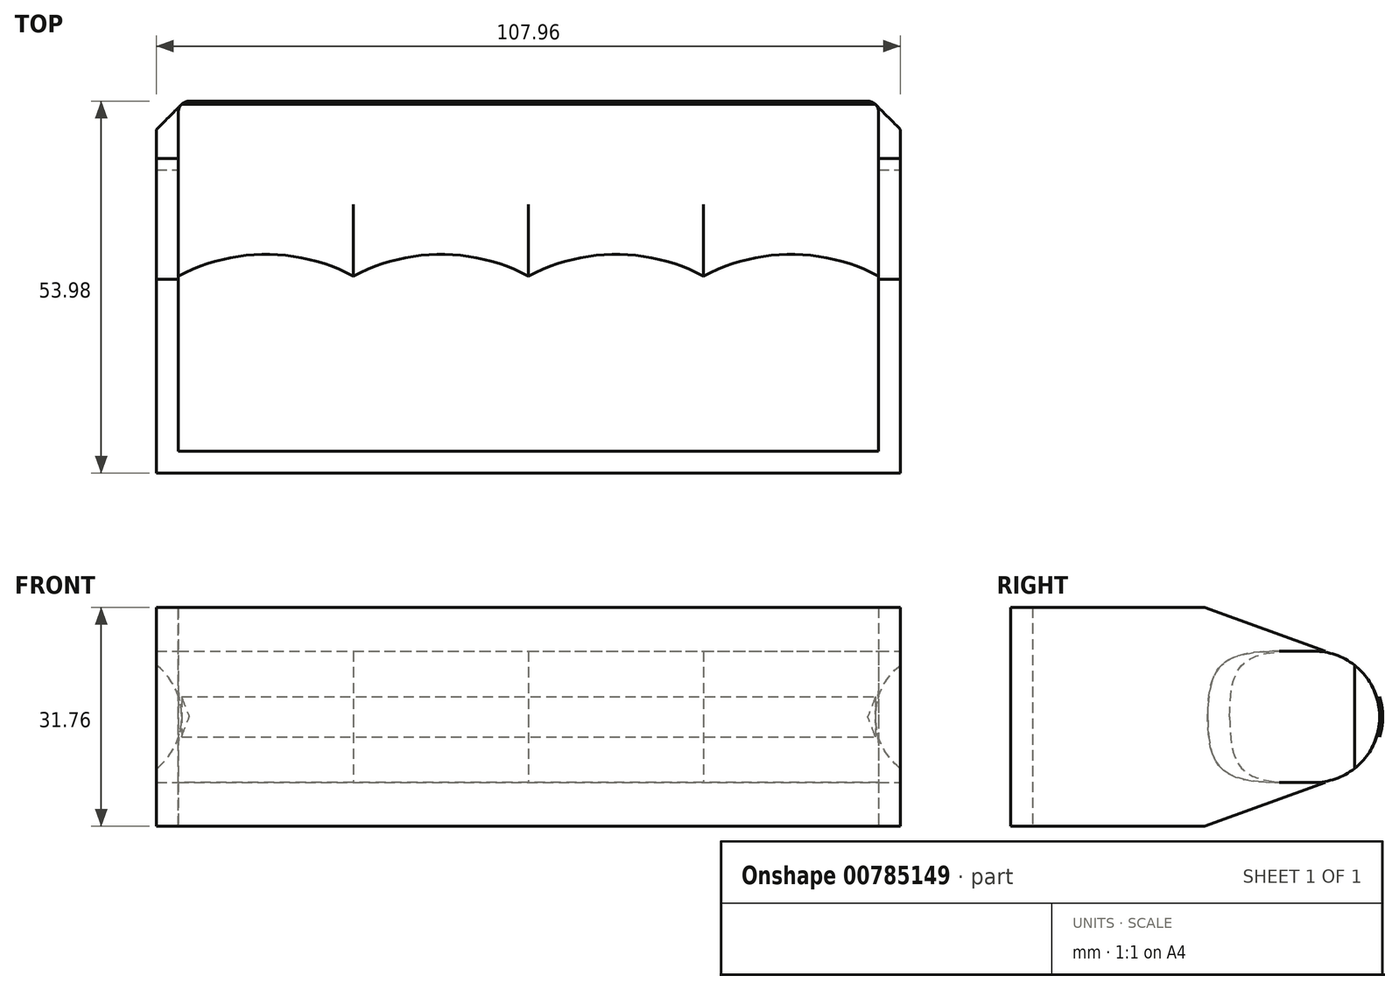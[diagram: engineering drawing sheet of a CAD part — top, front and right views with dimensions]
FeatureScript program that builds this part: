
annotation { "Feature Type Name" : "Feature", "Feature Type Description" : "" }
export const myFeature = defineFeature(function(context is Context, id is Id, definition is map)
    precondition{}
    {
        {
            var Q0;
            Q0=qCreatedBy(makeId("Top.planeOp"),FACE);
            var sketch = newSketch(context, id + "F0", { "sketchPlane" : qUnion([Q0])});
            skLineSegment(sketch, "E0.bottom", {"start": v(50.8, 25.4) * mm, "end": v(-50.8, 25.4) * mm, "construction": true});
            skLineSegment(sketch, "E0.top", {"start": v(49.21, 50.8) * mm, "end": v(-49.21, 50.8) * mm});
            skLineSegment(sketch, "E0.left", {"start": v(50.8, 25.4) * mm, "end": v(50.8, 49.21) * mm});
            skLineSegment(sketch, "E0.right", {"start": v(-50.8, 25.4) * mm, "end": v(-50.8, 49.21) * mm});
            skPoint(sketch, "E0.middle", {"position": v(0, 38.1) * mm});
            skPoint(sketch, "E1.visualSharp", {"position": v(50.8, 50.8) * mm});
            skArc(sketch, "E1.filletArc", {"start": v(50.8, 49.21) * mm, "mid": v(50.34, 50.34) * mm, "end": v(49.21, 50.8) * mm});
            skPoint(sketch, "E2.visualSharp", {"position": v(-50.8, 50.8) * mm});
            skArc(sketch, "E2.filletArc", {"start": v(-49.21, 50.8) * mm, "mid": v(-50.34, 50.34) * mm, "end": v(-50.8, 49.21) * mm});
            skArc(sketch, "E3", {"start": v(50.8, 25.4) * mm, "mid": v(38.1, 28.58) * mm, "end": v(25.4, 25.4) * mm});
            skArc(sketch, "E4", {"start": v(25.4, 25.4) * mm, "mid": v(12.7, 28.57) * mm, "end": v(0, 25.4) * mm});
            skArc(sketch, "E5", {"start": v(0, 25.4) * mm, "mid": v(-12.7, 28.57) * mm, "end": v(-25.4, 25.4) * mm});
            skArc(sketch, "E6", {"start": v(-50.8, 25.4) * mm, "mid": v(-38.1, 28.57) * mm, "end": v(-25.4, 25.4) * mm});
            skLineSegment(sketch, "E7.left", {"start": v(-50.8, 49.21) * mm, "end": v(-50.8, 0) * mm});
            skLineSegment(sketch, "E7.right", {"start": v(-53.98, 46.7) * mm, "end": v(-53.97, 0) * mm});
            skLineSegment(sketch, "E8.right", {"start": v(53.98, 46.7) * mm, "end": v(53.98, 0) * mm});
            skLineSegment(sketch, "E9.bottom", {"start": v(-50.8, 0) * mm, "end": v(50.8, 0) * mm});
            skLineSegment(sketch, "E9.top", {"start": v(-53.97, -3.17) * mm, "end": v(53.98, -3.17) * mm});
            skLineSegment(sketch, "E9.left", {"start": v(-53.97, 0) * mm, "end": v(-53.97, -3.17) * mm});
            skLineSegment(sketch, "E9.right", {"start": v(53.98, 0) * mm, "end": v(53.98, -3.17) * mm});
            skLineSegment(sketch, "E10", {"start": v(50.34, 50.34) * mm, "end": v(53.98, 46.7) * mm});
            skLineSegment(sketch, "E11.trimOffspring", {"start": v(50.8, 49.21) * mm, "end": v(50.8, 0) * mm});
            skLineSegment(sketch, "E12", {"start": v(-50.34, 50.34) * mm, "end": v(-53.98, 46.7) * mm});
            skSolve(sketch);
        }
        {
            var Q0;
            {var subQ6=sQuery(id+"F0.wireOp",EDGE,"E0.top");Q0=makeQuery(id+"F0.imprint","IMPRINT",FACE,{"disambiguationData":[TD([[makeQuery(id+"F0.imprint","IMPRINT",EDGE,{"derivedFrom":subQ6}),1.0]])]});}
            extrude(context, id + "F1", {"entities" : qUnion([Q0]), "depth" : 9.52 * mm, "offsetDistance" : 25.4 * mm, "hasSecondDirection" : true, "secondDirectionOppositeDirection" : true, "secondDirectionDepth" : 9.52 * mm});
        }
        {
            var Q0;
            Q0=makeQuery(id+"F0.imprint","IMPRINT",FACE,{"disambiguationData":[TD([[makeQuery(id+"F0.imprint","IMPRINT",EDGE,{"derivedFrom":sQuery(id+"F0.wireOp",EDGE,"E7.right")}),1.0]])]});
            extrude(context, id + "F2", {"entities" : qUnion([Q0]), "depth" : 15.88 * mm, "offsetDistance" : 25.4 * mm, "hasSecondDirection" : true, "secondDirectionOppositeDirection" : true, "secondDirectionDepth" : 15.88 * mm});
        }
        {
            var Q0;
            Q0=makeQuery(id+"F1.opExtrude","CAP_EDGE",EDGE,{"disambiguationData":[OSD([sQuery(id+"F0.wireOp",EDGE,"E0.top")])],"isStart":false});
            var Q1;
            Q1=makeQuery(id+"F1.opExtrude","CAP_EDGE",EDGE,{"disambiguationData":[OSD([sQuery(id+"F0.wireOp",EDGE,"E0.top")])],"isStart":true});
            fillet(context, id + "F3", {"entities" : qUnion([Q0, Q1]), "radius" : 9.52 * mm, "allowEdgeOverflow" : false});
        }
        {
            var Q0;
            Q0=makeQuery(id+"F1.opExtrude","CAP_EDGE",EDGE,{"disambiguationData":[OSD([sQuery(id+"F0.wireOp",EDGE,"E5")])],"isStart":true});
            var Q1;
            Q1=makeQuery(id+"F1.opExtrude","CAP_EDGE",EDGE,{"disambiguationData":[OSD([sQuery(id+"F0.wireOp",EDGE,"E6")])],"isStart":true});
            var Q2;
            Q2=makeQuery(id+"F1.opExtrude","CAP_EDGE",EDGE,{"disambiguationData":[OSD([sQuery(id+"F0.wireOp",EDGE,"E6")])],"isStart":false});
            var Q3;
            Q3=makeQuery(id+"F1.opExtrude","CAP_EDGE",EDGE,{"disambiguationData":[OSD([sQuery(id+"F0.wireOp",EDGE,"E5")])],"isStart":false});
            var Q4;
            Q4=makeQuery(id+"F1.opExtrude","CAP_EDGE",EDGE,{"disambiguationData":[OSD([sQuery(id+"F0.wireOp",EDGE,"E4")])],"isStart":true});
            var Q5;
            Q5=makeQuery(id+"F1.opExtrude","CAP_EDGE",EDGE,{"disambiguationData":[OSD([sQuery(id+"F0.wireOp",EDGE,"E4")])],"isStart":false});
            var Q6;
            Q6=makeQuery(id+"F1.opExtrude","CAP_EDGE",EDGE,{"disambiguationData":[OSD([sQuery(id+"F0.wireOp",EDGE,"E3")])],"isStart":true});
            var Q7;
            Q7=makeQuery(id+"F1.opExtrude","CAP_EDGE",EDGE,{"disambiguationData":[OSD([sQuery(id+"F0.wireOp",EDGE,"E3")])],"isStart":false});
            fillet(context, id + "F4", {"entities" : qUnion([Q0, Q1, Q2, Q3, Q4, Q5, Q6, Q7]), "radius" : 9.52 * mm, "rho" : 0.6, "crossSection" : FilletCrossSection.CONIC, "allowEdgeOverflow" : false});
        }
        {
            var Q0;
            Q0=qCreatedBy(makeId("Right.planeOp"),FACE);
            var sketch = newSketch(context, id + "F5", { "sketchPlane" : qUnion([Q0])});
            skLineSegment(sketch, "E13.bottom", {"start": v(50.34, 9.53) * mm, "end": v(24.94, 9.52) * mm});
            skLineSegment(sketch, "E13.top", {"start": v(50.34, 15.88) * mm, "end": v(24.94, 15.88) * mm});
            skLineSegment(sketch, "E13.left", {"start": v(50.34, 9.53) * mm, "end": v(50.34, 15.88) * mm});
            skLineSegment(sketch, "E13.right", {"start": v(24.94, 9.52) * mm, "end": v(24.94, 15.87) * mm, "construction": true});
            skLineSegment(sketch, "E14.bottom", {"start": v(50.34, -9.52) * mm, "end": v(24.94, -9.53) * mm});
            skLineSegment(sketch, "E14.top", {"start": v(50.34, -15.88) * mm, "end": v(24.94, -15.88) * mm});
            skLineSegment(sketch, "E14.left", {"start": v(50.34, -9.52) * mm, "end": v(50.34, -15.88) * mm});
            skLineSegment(sketch, "E14.right", {"start": v(24.94, -9.53) * mm, "end": v(24.94, -15.88) * mm, "construction": true});
            skArc(sketch, "E15", {"start": v(40.82, -9.53) * mm, "mid": v(50.34, 0) * mm, "end": v(40.82, 9.53) * mm});
            skLineSegment(sketch, "E16", {"start": v(50.34, 9.53) * mm, "end": v(50.34, -9.52) * mm});
            skLineSegment(sketch, "E17", {"start": v(44.06, 8.96) * mm, "end": v(24.94, 15.87) * mm});
            skLineSegment(sketch, "E18", {"start": v(24.94, -15.88) * mm, "end": v(44.06, -8.96) * mm});
            skSolve(sketch);
        }
        {
            var Q0;
            Q0 = qSketchRegion(id + "F5", true);
            extrude(context, id + "F6", {"entities" : qUnion([Q0]), "operationType" : NewBodyOperationType.REMOVE, "oppositeDirection" : true, "depth" : 76.2 * mm, "offsetDistance" : 25.4 * mm, "hasSecondDirection" : true, "secondDirectionOppositeDirection" : false, "secondDirectionDepth" : 76.2 * mm});
        }
    });
